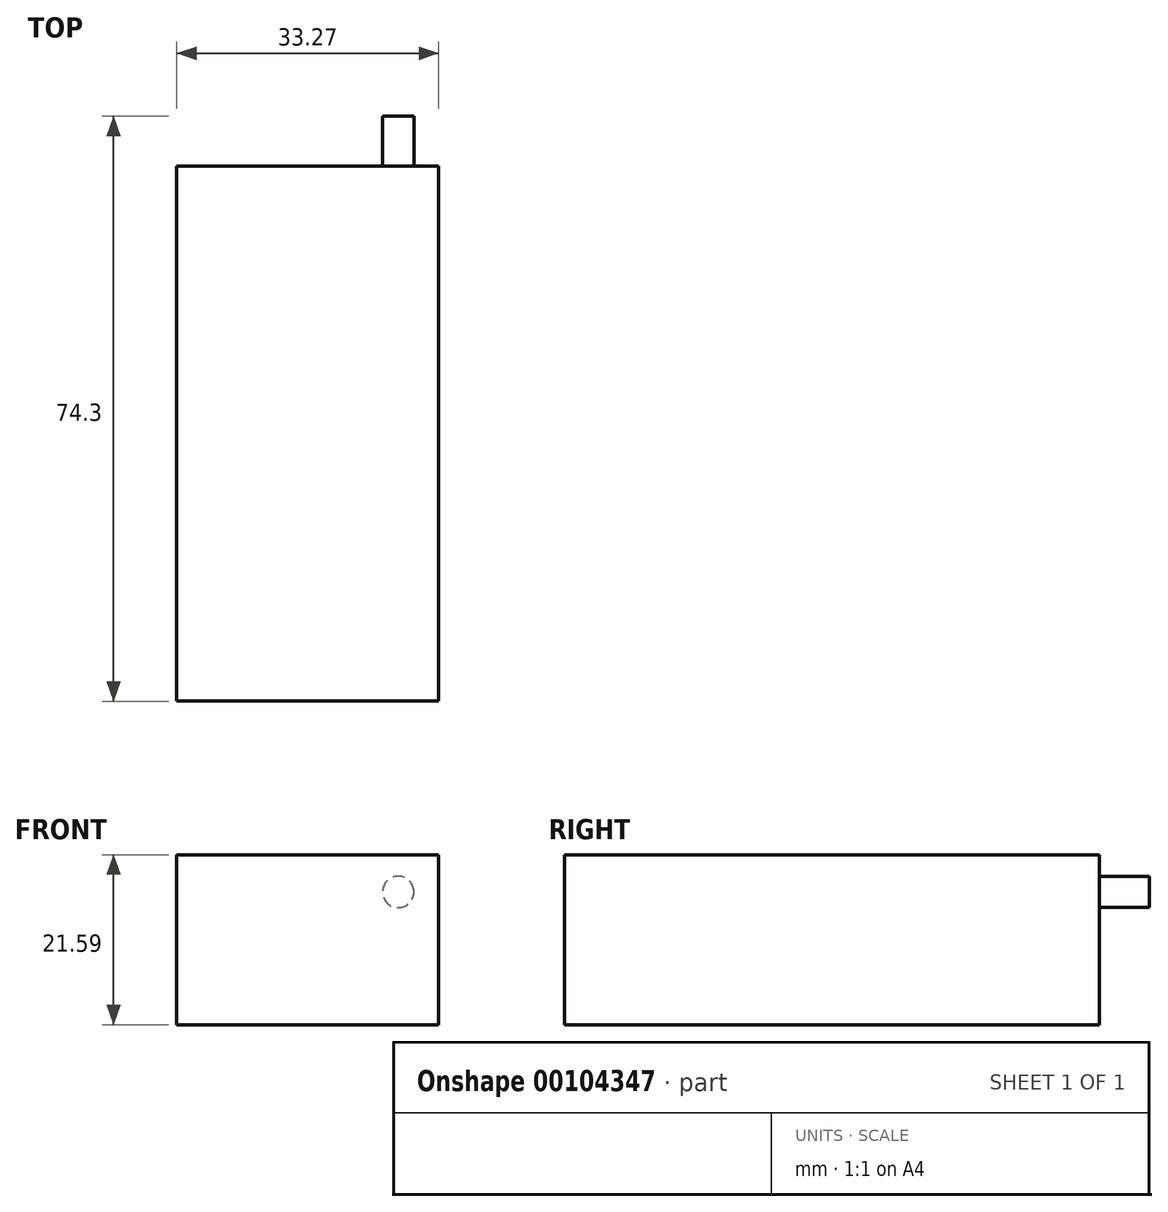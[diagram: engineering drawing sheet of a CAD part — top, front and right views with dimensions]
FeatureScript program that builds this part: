
annotation { "Feature Type Name" : "Feature", "Feature Type Description" : "" }
export const myFeature = defineFeature(function(context is Context, id is Id, definition is map)
    precondition{}
    {
        {
            var Q0;
            Q0=qCreatedBy(makeId("Front.planeOp"),FACE);
            var sketch = newSketch(context, id + "F0", { "sketchPlane" : qUnion([Q0])});
            skLineSegment(sketch, "E0.bottom", {"start": v(0, 0) * mm, "end": v(33.27, 0) * mm});
            skLineSegment(sketch, "E0.top", {"start": v(0, 21.6) * mm, "end": v(33.27, 21.6) * mm});
            skLineSegment(sketch, "E0.left", {"start": v(0, 0) * mm, "end": v(0, 21.6) * mm});
            skLineSegment(sketch, "E0.right", {"start": v(33.27, 0) * mm, "end": v(33.27, 21.6) * mm});
            skSolve(sketch);
        }
        {
            var Q0;
            Q0 = qSketchRegion(id + "F0", true);
            extrude(context, id + "F1", {"entities" : qUnion([Q0]), "depth" : 67.94 * mm});
        }
        {
            var Q0;
            Q0=makeQuery(id+"F1.opExtrude","CAP_FACE",FACE,{"disambiguationData":[OSD([sQuery(id+"F0.wireOp",EDGE,"E0.bottom"),sQuery(id+"F0.wireOp",EDGE,"E0.top"),sQuery(id+"F0.wireOp",EDGE,"E0.left"),sQuery(id+"F0.wireOp",EDGE,"E0.right")])],"isStart":true});
            var sketch = newSketch(context, id + "F2", { "sketchPlane" : qUnion([Q0])});
            skCircle(sketch, "E1", {"center": v(-28.14, 16.87) * mm, "radius": 1.99 * mm});
            skSolve(sketch);
        }
        {
            var Q0;
            Q0 = qSketchRegion(id + "F2", true);
            extrude(context, id + "F3", {"entities" : qUnion([Q0]), "operationType" : NewBodyOperationType.ADD, "depth" : 6.35 * mm});
        }
    });
